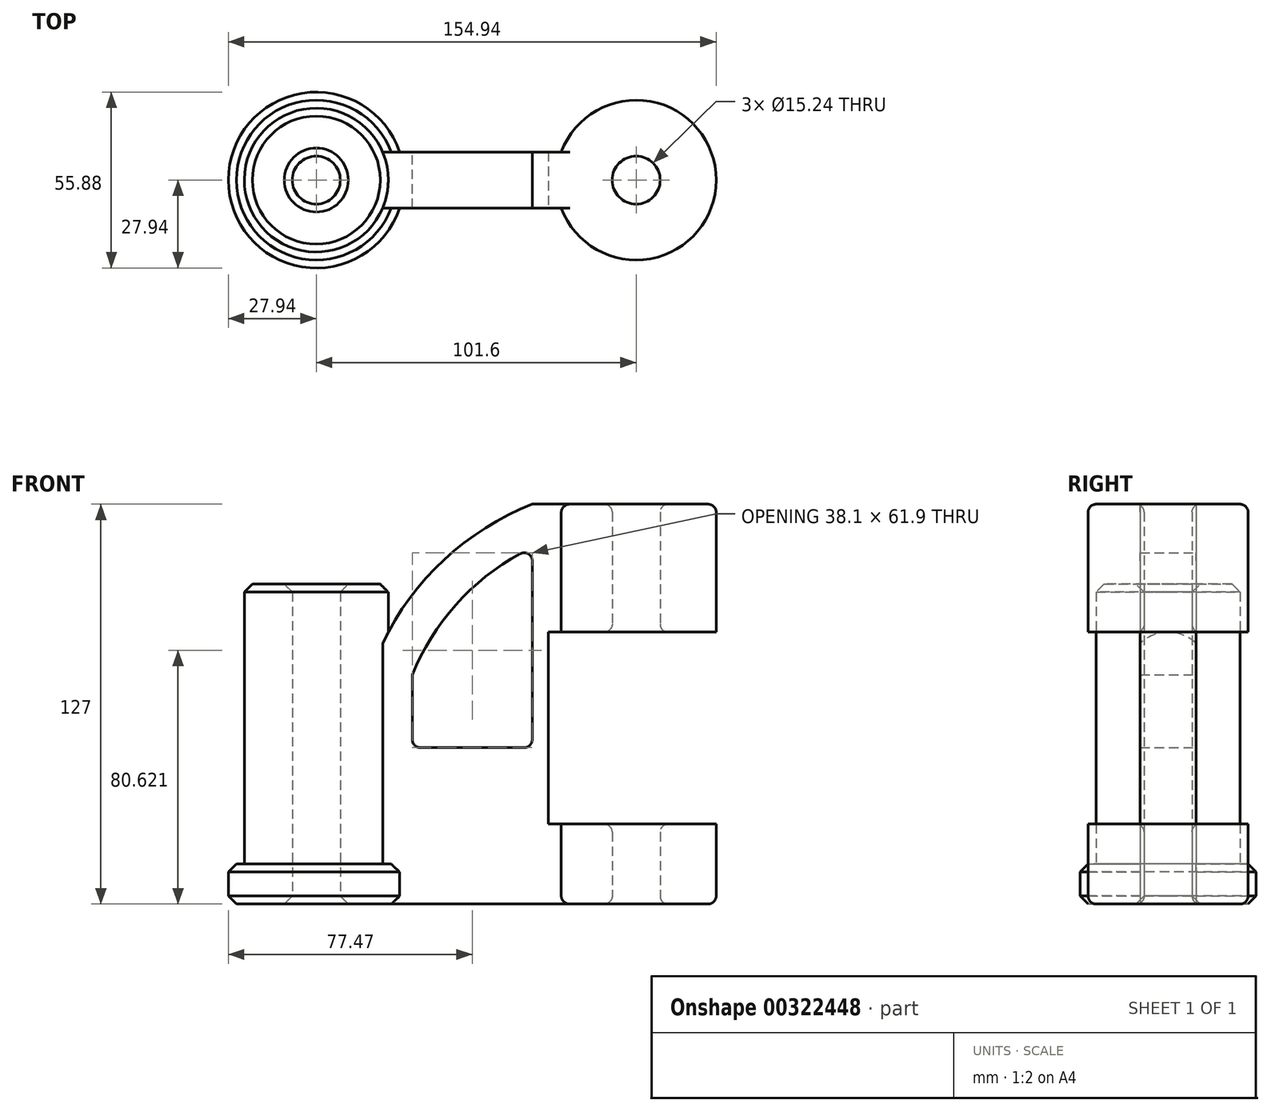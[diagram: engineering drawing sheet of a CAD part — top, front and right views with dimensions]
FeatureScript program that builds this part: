
annotation { "Feature Type Name" : "Feature", "Feature Type Description" : "" }
export const myFeature = defineFeature(function(context is Context, id is Id, definition is map)
    precondition{}
    {
        {
            var Q0;
            Q0=qCreatedBy(makeId("Top.planeOp"),FACE);
            var sketch = newSketch(context, id + "F0", { "sketchPlane" : qUnion([Q0])});
            skCircle(sketch, "E0", {"center": v(0, 0) * mm, "radius": 25.4 * mm});
            skCircle(sketch, "E1", {"center": v(0, 0) * mm, "radius": 7.62 * mm});
            skCircle(sketch, "E2", {"center": v(-101.6, 0) * mm, "radius": 7.62 * mm});
            skCircle(sketch, "E3", {"center": v(-101.6, 0) * mm, "radius": 22.86 * mm});
            skSolve(sketch);
        }
        {
            var Q0;
            Q0=makeQuery(id+"F0.imprint","IMPRINT",FACE,{"disambiguationData":[TD([[makeQuery(id+"F0.imprint","IMPRINT",EDGE,{"derivedFrom":sQuery(id+"F0.wireOp",EDGE,"E0")}),1.0]])]});
            extrude(context, id + "F1", {"entities" : qUnion([Q0]), "depth" : 127 * mm});
        }
        {
            var Q0;
            Q0=makeQuery(id+"F0.imprint","IMPRINT",FACE,{"disambiguationData":[TD([[makeQuery(id+"F0.imprint","IMPRINT",EDGE,{"derivedFrom":sQuery(id+"F0.wireOp",EDGE,"E2")}),-1.0]])]});
            extrude(context, id + "F2", {"entities" : qUnion([Q0]), "depth" : 101.6 * mm});
        }
        {
            var Q0;
            Q0=qCreatedBy(makeId("Front.planeOp"),FACE);
            var sketch = newSketch(context, id + "F3", { "sketchPlane" : qUnion([Q0])});
            skLineSegment(sketch, "E4", {"start": v(-20.32, 127) * mm, "end": v(-20.32, 0) * mm});
            skLineSegment(sketch, "E5", {"start": v(-20.32, 0) * mm, "end": v(-81.28, 0) * mm});
            skLineSegment(sketch, "E6", {"start": v(-81.28, 0) * mm, "end": v(-81.28, 81.28) * mm});
            skLineSegment(sketch, "E7", {"start": v(-20.32, 127) * mm, "end": v(-33.02, 127) * mm});
            skArc(sketch, "E8", {"start": v(-33.02, 127) * mm, "mid": v(-61.58, 108.82) * mm, "end": v(-81.28, 81.28) * mm});
            skArc(sketch, "E9.0", {"start": v(-33.02, 113.17) * mm, "mid": v(-55.88, 96.56) * mm, "end": v(-71.12, 72.77) * mm});
            skLineSegment(sketch, "E10", {"start": v(-33.02, 113.17) * mm, "end": v(-33.02, 49.67) * mm});
            skLineSegment(sketch, "E11", {"start": v(-33.02, 49.67) * mm, "end": v(-71.12, 49.67) * mm});
            skLineSegment(sketch, "E12", {"start": v(-71.12, 49.67) * mm, "end": v(-71.12, 72.77) * mm});
            skSolve(sketch);
        }
        {
            var Q0;
            Q0=makeQuery(id+"F3.imprint","IMPRINT",FACE,{"disambiguationData":[TD([[makeQuery(id+"F3.imprint","IMPRINT",EDGE,{"derivedFrom":sQuery(id+"F3.wireOp",EDGE,"E4")}),-1.0]])]});
            extrude(context, id + "F4", {"entities" : qUnion([Q0]), "operationType" : NewBodyOperationType.ADD, "depth" : 17.78 * mm, "symmetric" : true});
        }
        {
            var Q0;
            Q0=qCreatedBy(makeId("Front.planeOp"),FACE);
            var sketch = newSketch(context, id + "F5", { "sketchPlane" : qUnion([Q0])});
            skLineSegment(sketch, "E13.bottom", {"start": v(33.02, 86.36) * mm, "end": v(-27.94, 86.36) * mm});
            skLineSegment(sketch, "E13.top", {"start": v(33.02, 25.4) * mm, "end": v(-27.94, 25.4) * mm});
            skLineSegment(sketch, "E13.left", {"start": v(33.02, 86.36) * mm, "end": v(33.02, 25.4) * mm});
            skLineSegment(sketch, "E13.right", {"start": v(-27.94, 86.36) * mm, "end": v(-27.94, 25.4) * mm});
            skSolve(sketch);
        }
        {
            var Q0;
            Q0=makeQuery(id+"F5.imprint","IMPRINT",FACE,{"disambiguationData":[TD([[makeQuery(id+"F5.imprint","IMPRINT",EDGE,{"derivedFrom":sQuery(id+"F5.wireOp",EDGE,"E13.bottom")}),1.0]])]});
            extrude(context, id + "F6", {"entities" : qUnion([Q0]), "operationType" : NewBodyOperationType.REMOVE, "oppositeDirection" : true, "depth" : 101.6 * mm, "symmetric" : true});
        }
        {
            var Q0;
            Q0=makeQuery(id+"F1.opExtrude","CAP_EDGE",EDGE,{"disambiguationData":[OSD([sQuery(id+"F0.wireOp",EDGE,"E0")])],"isStart":false});
            var Q1;
            Q1=makeQuery(id+"F1.opExtrude","CAP_EDGE",EDGE,{"disambiguationData":[OSD([sQuery(id+"F0.wireOp",EDGE,"E0")])],"isStart":true});
            var Q2;
            Q2=makeQuery(id+"F6.boolean.opBoolean","INTERSECT",EDGE,{"derivedFrom":[makeQuery(id+"F1.opExtrude","SWEPT_FACE",FACE,{"disambiguationData":[OSD([sQuery(id+"F0.wireOp",EDGE,"E1")])]}),makeQuery(id+"F6.opExtrude","SWEPT_FACE",FACE,{"disambiguationData":[OSD([sQuery(id+"F5.wireOp",EDGE,"E13.bottom")])]})]});
            var Q3;
            Q3=makeQuery(id+"F1.opExtrude","CAP_EDGE",EDGE,{"disambiguationData":[OSD([sQuery(id+"F0.wireOp",EDGE,"E1")])],"isStart":true});
            var Q4;
            Q4=makeQuery(id+"F1.opExtrude","CAP_EDGE",EDGE,{"disambiguationData":[OSD([sQuery(id+"F0.wireOp",EDGE,"E1")])],"isStart":false});
            var Q5;
            Q5=makeQuery(id+"F6.boolean.opBoolean","INTERSECT",EDGE,{"derivedFrom":[makeQuery(id+"F1.opExtrude","SWEPT_FACE",FACE,{"disambiguationData":[OSD([sQuery(id+"F0.wireOp",EDGE,"E1")])]}),makeQuery(id+"F6.opExtrude","SWEPT_FACE",FACE,{"disambiguationData":[OSD([sQuery(id+"F5.wireOp",EDGE,"E13.top")])]})]});
            var Q6;
            Q6=makeQuery(id+"F4.opExtrude","SWEPT_EDGE",EDGE,{"disambiguationData":[OSD([sQuery(id+"F3.wireOp",EDGE,"E10"),sQuery(id+"F3.wireOp",EDGE,"E11")])]});
            var Q7;
            Q7=makeQuery(id+"F4.opExtrude","SWEPT_EDGE",EDGE,{"disambiguationData":[OSD([sQuery(id+"F3.wireOp",EDGE,"E11"),sQuery(id+"F3.wireOp",EDGE,"E12")])]});
            var Q8;
            Q8=makeQuery(id+"F4.opExtrude","SWEPT_EDGE",EDGE,{"disambiguationData":[OSD([sQuery(id+"F3.wireOp",EDGE,"E9.0"),sQuery(id+"F3.wireOp",EDGE,"E10")])]});
            fillet(context, id + "F7", {"entities" : qUnion([Q0, Q1, Q2, Q3, Q4, Q5, Q6, Q7, Q8]), "radius" : 2.54 * mm, "tangentPropagation" : true, "allowEdgeOverflow" : false});
        }
        {
            var Q0;
            Q0=qCreatedBy(makeId("Top.planeOp"),FACE);
            var sketch = newSketch(context, id + "F8", { "sketchPlane" : qUnion([Q0])});
            skCircle(sketch, "E14.0", {"center": v(-101.6, 0) * mm, "radius": 22.86 * mm});
            skCircle(sketch, "E15.0", {"center": v(-101.6, 0) * mm, "radius": 27.94 * mm});
            skSolve(sketch);
        }
        {
            var Q0;
            Q0 = qSketchRegion(id + "F8", true);
            extrude(context, id + "F9", {"entities" : qUnion([Q0]), "operationType" : NewBodyOperationType.ADD, "depth" : 12.7 * mm});
        }
        {
            var Q0;
            Q0=makeQuery(id+"F9.opExtrude","CAP_EDGE",EDGE,{"disambiguationData":[OSD([sQuery(id+"F8.wireOp",EDGE,"E15.0")])],"isStart":true});
            var Q1;
            Q1=makeQuery(id+"F2.opExtrude","CAP_EDGE",EDGE,{"disambiguationData":[OSD([sQuery(id+"F0.wireOp",EDGE,"E2")])],"isStart":true});
            var Q2;
            Q2=makeQuery(id+"F9.opExtrude","CAP_EDGE",EDGE,{"disambiguationData":[OSD([sQuery(id+"F8.wireOp",EDGE,"E15.0")])],"isStart":false});
            var Q3;
            Q3=makeQuery(id+"F2.opExtrude","CAP_EDGE",EDGE,{"disambiguationData":[OSD([sQuery(id+"F0.wireOp",EDGE,"E3")])],"isStart":false});
            var Q4;
            Q4=makeQuery(id+"F2.opExtrude","CAP_EDGE",EDGE,{"disambiguationData":[OSD([sQuery(id+"F0.wireOp",EDGE,"E2")])],"isStart":false});
            chamfer(context, id + "F10", {"entities" : qUnion([Q0, Q1, Q2, Q3, Q4]), "width" : 2.54 * mm, "tangentPropagation" : true});
        }
    });
